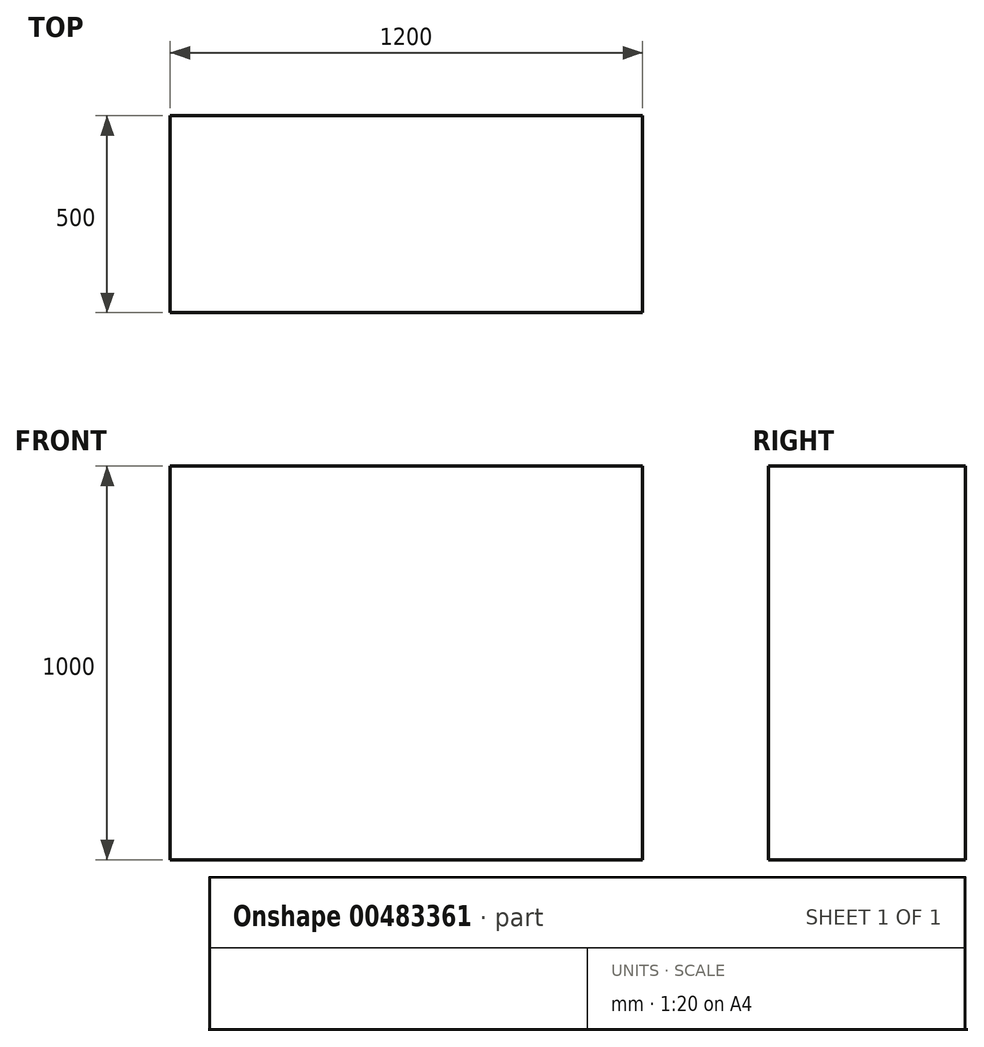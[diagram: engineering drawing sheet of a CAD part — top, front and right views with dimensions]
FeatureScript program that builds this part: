
annotation { "Feature Type Name" : "Feature", "Feature Type Description" : "" }
export const myFeature = defineFeature(function(context is Context, id is Id, definition is map)
    precondition{}
    {
        {
            var Q0;
            Q0=qCreatedBy(makeId("Top.planeOp"),FACE);
            var sketch = newSketch(context, id + "F0", { "sketchPlane" : qUnion([Q0])});
            skLineSegment(sketch, "E0", {"start": v(0, 0) * mm, "end": v(0, 500) * mm});
            skLineSegment(sketch, "E1", {"start": v(0, 500) * mm, "end": v(1200, 500) * mm});
            skLineSegment(sketch, "E2", {"start": v(1200, 500) * mm, "end": v(1200, 0) * mm});
            skLineSegment(sketch, "E3", {"start": v(1200, 0) * mm, "end": v(0, 0) * mm});
            skSolve(sketch);
        }
        {
            var Q0;
            Q0=makeQuery(id+"F0.imprint","IMPRINT",FACE,{"disambiguationData":[TD([[makeQuery(id+"F0.imprint","IMPRINT",EDGE,{"derivedFrom":sQuery(id+"F0.wireOp",EDGE,"E0")}),-1.0]])]});
            extrude(context, id + "F1", {"entities" : qUnion([Q0]), "depth" : 950 * mm});
        }
        {
            var Q0;
            Q0=makeQuery(id+"F1.opExtrude","CAP_FACE",FACE,{"disambiguationData":[OSD([sQuery(id+"F0.wireOp",EDGE,"E0"),sQuery(id+"F0.wireOp",EDGE,"E1"),sQuery(id+"F0.wireOp",EDGE,"E2"),sQuery(id+"F0.wireOp",EDGE,"E3")])],"isStart":true});
            extrude(context, id + "F2", {"entities" : qUnion([Q0]), "operationType" : NewBodyOperationType.ADD, "depth" : 25 * mm, "offsetDistance" : 25 * mm});
        }
        {
            var Q0;
            Q0=makeQuery(id+"F2.opExtrude","CAP_FACE",FACE,{"disambiguationData":[OSD([sQuery(id+"F0.wireOp",EDGE,"E0"),sQuery(id+"F0.wireOp",EDGE,"E1"),sQuery(id+"F0.wireOp",EDGE,"E2"),sQuery(id+"F0.wireOp",EDGE,"E3")])],"isStart":false});
            extrude(context, id + "F3", {"entities" : qUnion([Q0]), "operationType" : NewBodyOperationType.ADD, "depth" : 25 * mm, "offsetDistance" : 25 * mm});
        }
    });
